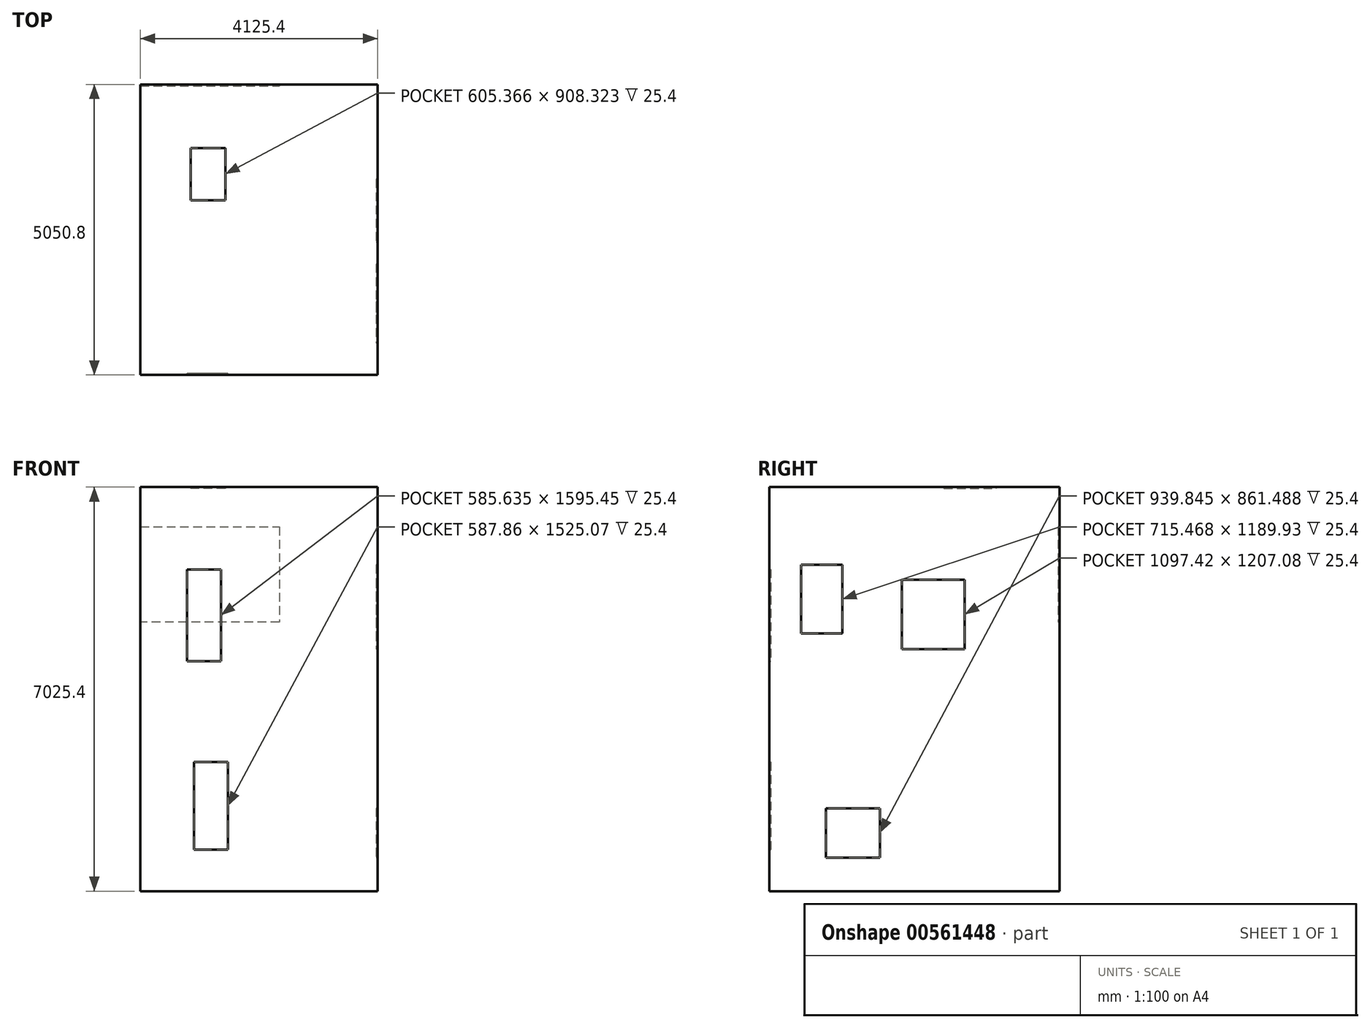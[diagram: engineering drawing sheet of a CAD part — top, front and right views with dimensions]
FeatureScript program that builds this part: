
annotation { "Feature Type Name" : "Feature", "Feature Type Description" : "" }
export const myFeature = defineFeature(function(context is Context, id is Id, definition is map)
    precondition{}
    {
        {
            var Q0;
            Q0=qCreatedBy(makeId("Right.planeOp"),FACE);
            var sketch = newSketch(context, id + "F0", { "sketchPlane" : qUnion([Q0])});
            skLineSegment(sketch, "E0.bottom", {"start": v(-2500, 3500) * mm, "end": v(2500, 3500) * mm});
            skLineSegment(sketch, "E0.top", {"start": v(-2500, -3500) * mm, "end": v(2500, -3500) * mm});
            skLineSegment(sketch, "E0.left", {"start": v(-2500, 3500) * mm, "end": v(-2500, -3500) * mm});
            skLineSegment(sketch, "E0.right", {"start": v(2500, 3500) * mm, "end": v(2500, -3500) * mm});
            skPoint(sketch, "E0.middle", {"position": v(0, 0) * mm});
            skSolve(sketch);
        }
        {
            var Q0;
            Q0 = qSketchRegion(id + "F0", true);
            extrude(context, id + "F1", {"entities" : qUnion([Q0]), "depth" : 4100 * mm, "offsetDistance" : 25.4 * mm});
        }
        {
            var Q0;
            Q0=makeQuery(id+"F1.opExtrude","CAP_FACE",FACE,{"disambiguationData":[OSD([sQuery(id+"F0.wireOp",EDGE,"E0.bottom"),sQuery(id+"F0.wireOp",EDGE,"E0.top"),sQuery(id+"F0.wireOp",EDGE,"E0.left"),sQuery(id+"F0.wireOp",EDGE,"E0.right")])],"isStart":false});
            var sketch = newSketch(context, id + "F2", { "sketchPlane" : qUnion([Q0])});
            skLineSegment(sketch, "E1.bottom", {"start": v(-598.93, -2058.75) * mm, "end": v(-1538.77, -2058.75) * mm});
            skLineSegment(sketch, "E1.top", {"start": v(-598.93, -2920.24) * mm, "end": v(-1538.77, -2920.24) * mm});
            skLineSegment(sketch, "E1.left", {"start": v(-598.93, -2058.75) * mm, "end": v(-598.93, -2920.24) * mm});
            skLineSegment(sketch, "E1.right", {"start": v(-1538.77, -2058.75) * mm, "end": v(-1538.77, -2920.24) * mm});
            skPoint(sketch, "E1.middle", {"position": v(-1068.85, -2489.5) * mm});
            skLineSegment(sketch, "E2.bottom", {"start": v(-1254.35, 2171.72) * mm, "end": v(-1969.82, 2171.72) * mm});
            skLineSegment(sketch, "E2.top", {"start": v(-1254.35, 981.8) * mm, "end": v(-1969.82, 981.8) * mm});
            skLineSegment(sketch, "E2.left", {"start": v(-1254.35, 2171.72) * mm, "end": v(-1254.35, 981.8) * mm});
            skLineSegment(sketch, "E2.right", {"start": v(-1969.82, 2171.72) * mm, "end": v(-1969.82, 981.8) * mm});
            skPoint(sketch, "E2.middle", {"position": v(-1612.09, 1576.76) * mm});
            skLineSegment(sketch, "E3.bottom", {"start": v(877.04, 1916.15) * mm, "end": v(-220.38, 1916.15) * mm});
            skLineSegment(sketch, "E3.top", {"start": v(877.04, 709.06) * mm, "end": v(-220.38, 709.06) * mm});
            skLineSegment(sketch, "E3.left", {"start": v(877.04, 1916.15) * mm, "end": v(877.04, 709.06) * mm});
            skLineSegment(sketch, "E3.right", {"start": v(-220.38, 1916.15) * mm, "end": v(-220.38, 709.06) * mm});
            skPoint(sketch, "E3.middle", {"position": v(328.33, 1312.6) * mm});
            skLineSegment(sketch, "E4.bottom", {"start": v(-2500, -3500) * mm, "end": v(2500, -3500) * mm});
            skLineSegment(sketch, "E4.top", {"start": v(-2500, 3500) * mm, "end": v(2500, 3500) * mm});
            skLineSegment(sketch, "E4.left", {"start": v(-2500, -3500) * mm, "end": v(-2500, 3500) * mm});
            skLineSegment(sketch, "E4.right", {"start": v(2500, -3500) * mm, "end": v(2500, 3500) * mm});
            skSolve(sketch);
        }
        {
            var Q0;
            Q0 = qSketchRegion(id + "F2", true);
            extrude(context, id + "F3", {"entities" : qUnion([Q0]), "operationType" : NewBodyOperationType.ADD, "depth" : 25.4 * mm, "offsetDistance" : 25.4 * mm});
        }
        {
            var Q0;
            Q0=makeQuery(id+"F3.boolean.opBoolean","MERGE",FACE,{"derivedFrom":[makeQuery(id+"F1.opExtrude","SWEPT_FACE",FACE,{"disambiguationData":[OSD([sQuery(id+"F0.wireOp",EDGE,"E0.right")])]}),makeQuery(id+"F3.opExtrude","SWEPT_FACE",FACE,{"disambiguationData":[OSD([sQuery(id+"F2.wireOp",EDGE,"E4.right")])]})]});
            var sketch = newSketch(context, id + "F4", { "sketchPlane" : qUnion([Q0])});
            skLineSegment(sketch, "E5", {"start": v(0, 1175.94) * mm, "end": v(0, -3500) * mm});
            skLineSegment(sketch, "E6", {"start": v(0, -3500) * mm, "end": v(-4125.4, -3500) * mm});
            skLineSegment(sketch, "E7", {"start": v(-4125.4, -3500) * mm, "end": v(-4125.4, 3500) * mm});
            skLineSegment(sketch, "E8", {"start": v(-4125.4, 3500) * mm, "end": v(0, 3500) * mm});
            skLineSegment(sketch, "E9", {"start": v(0, 3500) * mm, "end": v(0, 2834.47) * mm});
            skLineSegment(sketch, "E10", {"start": v(0, 2834.47) * mm, "end": v(-2418.46, 2834.47) * mm});
            skLineSegment(sketch, "E11", {"start": v(-2418.46, 2834.47) * mm, "end": v(-2418.46, 1175.94) * mm});
            skLineSegment(sketch, "E12", {"start": v(-2418.46, 1175.94) * mm, "end": v(0, 1175.94) * mm});
            skSolve(sketch);
        }
        {
            var Q0;
            Q0 = qSketchRegion(id + "F4", true);
            extrude(context, id + "F5", {"entities" : qUnion([Q0]), "operationType" : NewBodyOperationType.ADD, "depth" : 25.4 * mm, "offsetDistance" : 25.4 * mm});
        }
        {
            var Q0;
            Q0=makeQuery(id+"F5.boolean.opBoolean","MERGE",FACE,{"derivedFrom":[makeQuery(id+"F3.boolean.opBoolean","MERGE",FACE,{"derivedFrom":[makeQuery(id+"F1.opExtrude","SWEPT_FACE",FACE,{"disambiguationData":[OSD([sQuery(id+"F0.wireOp",EDGE,"E0.bottom")])]}),makeQuery(id+"F3.opExtrude","SWEPT_FACE",FACE,{"disambiguationData":[OSD([sQuery(id+"F2.wireOp",EDGE,"E4.top")])]})]}),makeQuery(id+"F5.opExtrude","SWEPT_FACE",FACE,{"disambiguationData":[OSD([sQuery(id+"F4.wireOp",EDGE,"E8")])]})]});
            var sketch = newSketch(context, id + "F6", { "sketchPlane" : qUnion([Q0])});
            skLineSegment(sketch, "E13.bottom", {"start": v(1478.88, 511.88) * mm, "end": v(873.51, 511.88) * mm});
            skLineSegment(sketch, "E13.top", {"start": v(1478.88, 1420.2) * mm, "end": v(873.51, 1420.2) * mm});
            skLineSegment(sketch, "E13.left", {"start": v(1478.88, 511.88) * mm, "end": v(1478.88, 1420.2) * mm});
            skLineSegment(sketch, "E13.right", {"start": v(873.51, 511.88) * mm, "end": v(873.51, 1420.2) * mm});
            skLineSegment(sketch, "E14.bottom", {"start": v(4125.4, -2500) * mm, "end": v(0, -2500) * mm});
            skLineSegment(sketch, "E14.top", {"start": v(4125.4, 2525.4) * mm, "end": v(0, 2525.4) * mm});
            skLineSegment(sketch, "E14.left", {"start": v(4125.4, -2500) * mm, "end": v(4125.4, 2525.4) * mm});
            skLineSegment(sketch, "E14.right", {"start": v(0, -2500) * mm, "end": v(0, 2525.4) * mm});
            skSolve(sketch);
        }
        {
            var Q0;
            Q0 = qSketchRegion(id + "F6", true);
            extrude(context, id + "F7", {"entities" : qUnion([Q0]), "operationType" : NewBodyOperationType.ADD, "depth" : 25.4 * mm, "offsetDistance" : 25.4 * mm});
        }
        {
            var Q0;
            Q0=makeQuery(id+"F7.boolean.opBoolean","MERGE",FACE,{"derivedFrom":[makeQuery(id+"F3.boolean.opBoolean","MERGE",FACE,{"derivedFrom":[makeQuery(id+"F1.opExtrude","SWEPT_FACE",FACE,{"disambiguationData":[OSD([sQuery(id+"F0.wireOp",EDGE,"E0.left")])]}),makeQuery(id+"F3.opExtrude","SWEPT_FACE",FACE,{"disambiguationData":[OSD([sQuery(id+"F2.wireOp",EDGE,"E4.left")])]})]}),makeQuery(id+"F7.opExtrude","SWEPT_FACE",FACE,{"disambiguationData":[OSD([sQuery(id+"F6.wireOp",EDGE,"E14.bottom")])]})]});
            var sketch = newSketch(context, id + "F8", { "sketchPlane" : qUnion([Q0])});
            skLineSegment(sketch, "E15.bottom", {"start": v(4125.4, 3525.4) * mm, "end": v(0, 3525.4) * mm});
            skLineSegment(sketch, "E15.top", {"start": v(4125.4, -3500) * mm, "end": v(0, -3500) * mm});
            skLineSegment(sketch, "E15.left", {"start": v(4125.4, 3525.4) * mm, "end": v(4125.4, -3500) * mm});
            skLineSegment(sketch, "E15.right", {"start": v(0, 3525.4) * mm, "end": v(0, -3500) * mm});
            skLineSegment(sketch, "E16.bottom", {"start": v(1399.71, 2093.34) * mm, "end": v(814.07, 2093.34) * mm});
            skLineSegment(sketch, "E16.top", {"start": v(1399.71, 497.89) * mm, "end": v(814.07, 497.89) * mm});
            skLineSegment(sketch, "E16.left", {"start": v(1399.71, 2093.34) * mm, "end": v(1399.71, 497.89) * mm});
            skLineSegment(sketch, "E16.right", {"start": v(814.07, 2093.34) * mm, "end": v(814.07, 497.89) * mm});
            skLineSegment(sketch, "E17.bottom", {"start": v(1523.18, -1254.55) * mm, "end": v(935.32, -1254.55) * mm});
            skLineSegment(sketch, "E17.top", {"start": v(1523.18, -2779.62) * mm, "end": v(935.32, -2779.62) * mm});
            skLineSegment(sketch, "E17.left", {"start": v(1523.18, -1254.55) * mm, "end": v(1523.18, -2779.62) * mm});
            skLineSegment(sketch, "E17.right", {"start": v(935.32, -1254.55) * mm, "end": v(935.32, -2779.62) * mm});
            skSolve(sketch);
        }
        {
            var Q0;
            Q0 = qSketchRegion(id + "F8", true);
            extrude(context, id + "F9", {"entities" : qUnion([Q0]), "operationType" : NewBodyOperationType.ADD, "depth" : 25.4 * mm, "offsetDistance" : 25.4 * mm});
        }
    });
